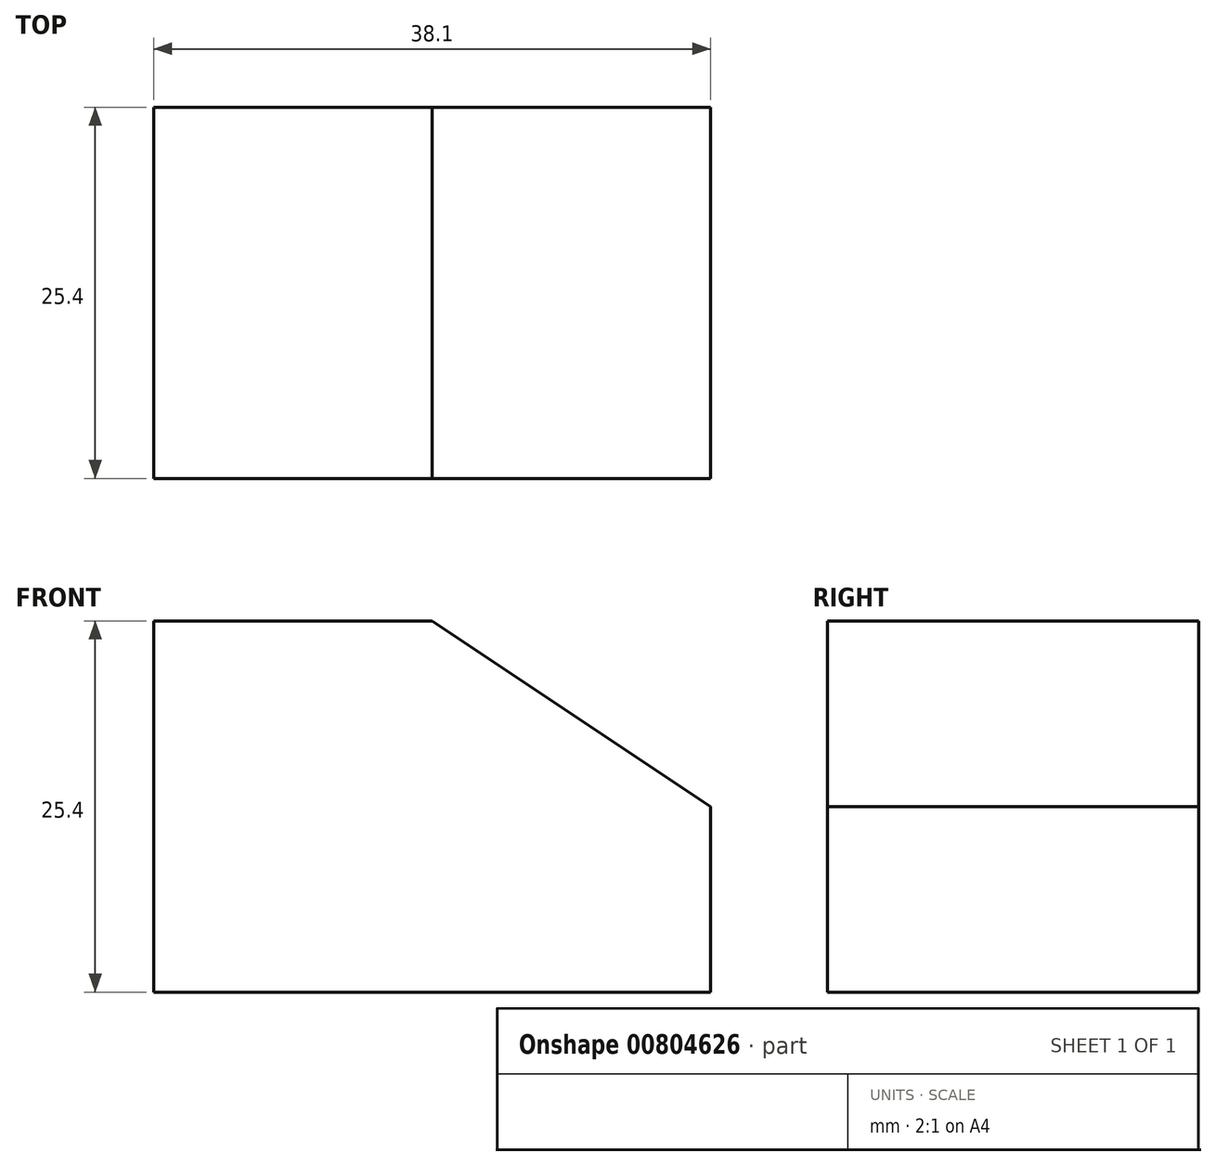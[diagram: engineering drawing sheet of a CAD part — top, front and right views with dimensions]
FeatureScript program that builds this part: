
annotation { "Feature Type Name" : "Feature", "Feature Type Description" : "" }
export const myFeature = defineFeature(function(context is Context, id is Id, definition is map)
    precondition{}
    {
        {
            var Q0;
            Q0=qCreatedBy(makeId("Front.planeOp"),FACE);
            var sketch = newSketch(context, id + "F0", { "sketchPlane" : qUnion([Q0])});
            skLineSegment(sketch, "E0", {"start": v(0, 0) * mm, "end": v(38.1, 0) * mm});
            skLineSegment(sketch, "E1", {"start": v(38.1, 0) * mm, "end": v(38.1, 12.7) * mm});
            skLineSegment(sketch, "E2", {"start": v(0, 0) * mm, "end": v(0, 25.4) * mm});
            skLineSegment(sketch, "E3", {"start": v(0, 25.4) * mm, "end": v(19.05, 25.4) * mm});
            skLineSegment(sketch, "E4", {"start": v(19.05, 25.4) * mm, "end": v(38.1, 12.7) * mm});
            skSolve(sketch);
        }
        {
            var Q0;
            Q0=makeQuery(id+"F0.imprint","IMPRINT",FACE,{"disambiguationData":[TD([[makeQuery(id+"F0.imprint","IMPRINT",EDGE,{"derivedFrom":sQuery(id+"F0.wireOp",EDGE,"E0")}),1.0]])]});
            extrude(context, id + "F1", {"entities" : qUnion([Q0]), "depth" : 25.4 * mm, "offsetDistance" : 25.4 * mm});
        }
    });
